# Revit family: Stex 45 Montageplatte MTB M12x 40
name_source: partatom
category: HLS-Bauteile
revit_build: Autodesk Revit 2017 (Build: 20190507_1515(x64)
units: mm (PartAtom-declared; Revit-internal decimal feet)

## family parameters
Arbeitsebenenbasiert = Ja
Beim Laden mit Abzugskörper schneiden = Nein
Bemaßung runder Anschluss = Durchmesser verwenden
Gemeinsam genutzt = Ja
Immer vertikal = Nein
Raumberechnungspunkt = Nein
Teiletyp = Normal

## types (1)
- Stex 45 Montageplatte MTB M12x 40
    Abmessung = M12 x 40 mm
    Anzugsmoment = 0.00 kN-m
    Artikelnummer = 1280001
    EAN = 4250928424655
    Fabrikat = MEFA
    Festigkeitsklasse = 8.8
    Firma = MEFA Befestigungs- und Montagesysteme GmbH
    Gewicht = 0.10 kg
    Gewicht pro Bauteil = 0.10 kg
    Gewinde = M12
    Kurztext1 = Stex Montagebolzen MTB 45
    Kurztext2 = M12 x 40 mm
    Länge Gewinde = 40 mm  [stored 0.131234 ft]
    Material = Stahl
    Mengeneinheit = St
    Nutzlänge = 25 mm
    Oberflaeche = galvanisch verzinkt
    Profiltyp = 45
    Vorgabe-Ansicht = 1219 mm
    vpe = 40 St

note: [stored X ft] marks values corroborated as IEEE doubles in the binary element streams (Revit-internal decimal feet)

## geometry (parser evidence)
native form markers: Sweep x3
no freeform markers — native parametric forms only
